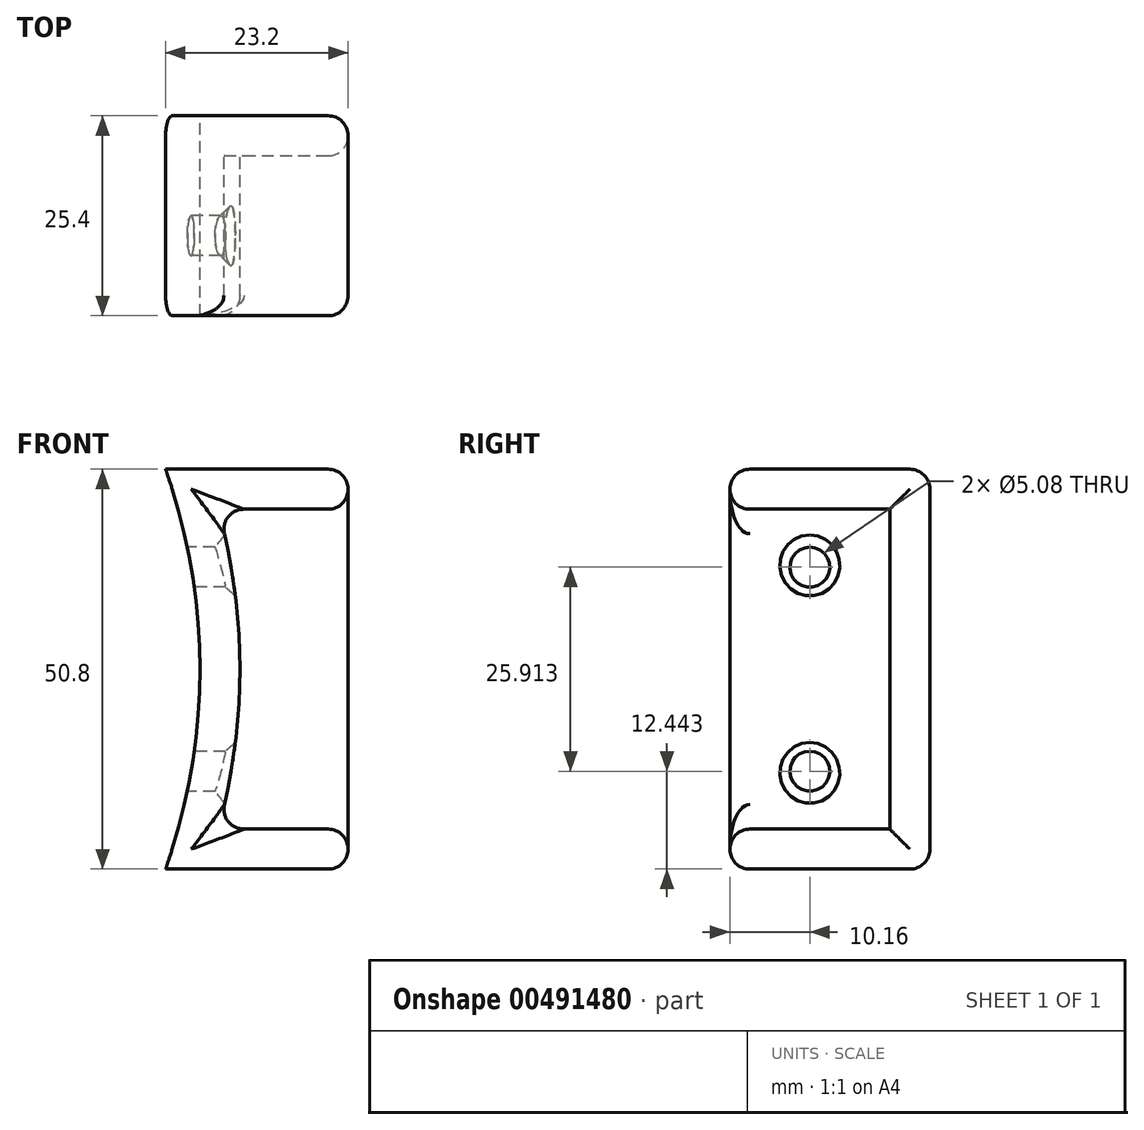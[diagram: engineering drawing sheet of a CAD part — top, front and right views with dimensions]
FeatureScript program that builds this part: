
annotation { "Feature Type Name" : "Feature", "Feature Type Description" : "" }
export const myFeature = defineFeature(function(context is Context, id is Id, definition is map)
    precondition{}
    {
        {
            var Q0;
            Q0=qCreatedBy(makeId("Front.planeOp"),FACE);
            var sketch = newSketch(context, id + "F0", { "sketchPlane" : qUnion([Q0])});
            skArc(sketch, "E0", {"start": v(71.84, -25.4) * mm, "mid": v(76.2, 0) * mm, "end": v(71.84, 25.4) * mm});
            skLineSegment(sketch, "E1", {"start": v(71.84, 25.4) * mm, "end": v(95.04, 25.4) * mm});
            skLineSegment(sketch, "E2", {"start": v(95.04, 25.4) * mm, "end": v(95.04, -25.4) * mm});
            skLineSegment(sketch, "E3", {"start": v(95.04, -25.4) * mm, "end": v(71.84, -25.4) * mm});
            skArc(sketch, "E4", {"start": v(78.52, -20.32) * mm, "mid": v(81.28, 0) * mm, "end": v(78.52, 20.32) * mm});
            skLineSegment(sketch, "E5", {"start": v(78.52, -20.32) * mm, "end": v(95.04, -20.32) * mm});
            skLineSegment(sketch, "E6", {"start": v(78.52, 20.32) * mm, "end": v(95.04, 20.32) * mm});
            skPoint(sketch, "E7.orphan", {"position": v(76.92, 25.4) * mm});
            skPoint(sketch, "E8.orphan", {"position": v(76.92, -25.4) * mm});
            skSolve(sketch);
        }
        {
            var Q0;
            Q0=makeQuery(id+"F0.imprint","IMPRINT",FACE,{"disambiguationData":[TD([[makeQuery(id+"F0.imprint","IMPRINT",EDGE,{"derivedFrom":sQuery(id+"F0.wireOp",EDGE,"E0")}),-1.0]])]});
            extrude(context, id + "F1", {"entities" : qUnion([Q0]), "depth" : 25.4 * mm});
        }
        {
            var Q0;
            Q0=makeQuery(id+"F0.imprint","IMPRINT",FACE,{"disambiguationData":[TD([[makeQuery(id+"F0.imprint","IMPRINT",EDGE,{"derivedFrom":sQuery(id+"F0.wireOp",EDGE,"E4")}),-1.0]])]});
            extrude(context, id + "F2", {"entities" : qUnion([Q0]), "operationType" : NewBodyOperationType.ADD, "depth" : 5.08 * mm});
        }
        {
            var Q0;
            Q0=makeQuery(id+"F2.opExtrude","CAP_EDGE",EDGE,{"disambiguationData":[OSD([sQuery(id+"F0.wireOp",EDGE,"E2")])],"isStart":false});
            fillet(context, id + "F3", {"entities" : qUnion([Q0]), "radius" : 2.54 * mm, "tangentPropagation" : true, "allowEdgeOverflow" : false});
        }
        {
            var Q0;
            Q0=makeQuery(id+"F1.opExtrude","SWEPT_EDGE",EDGE,{"disambiguationData":[OSD([sQuery(id+"F0.wireOp",EDGE,"E2"),sQuery(id+"F0.wireOp",EDGE,"E5")])]});
            var Q1;
            {var subQ0=sQuery(id+"F0.wireOp",EDGE,"E2");Q1=makeQuery(id+"F1.opExtrude","CAP_EDGE",EDGE,{"disambiguationData":[OSD([subQ0]),TDD([makeQuery(id+"F0.imprint","IMPRINT",EDGE,{"disambiguationData":[TD([[makeQuery(id+"F0.imprint","INTERSECT",VERTEX,{"derivedFrom":[subQ0,sQuery(id+"F0.wireOp",EDGE,"E3")]}),1.0]])],"derivedFrom":subQ0})])],"isStart":false});}
            var Q2;
            Q2=makeQuery(id+"F1.opExtrude","SWEPT_EDGE",EDGE,{"disambiguationData":[OSD([sQuery(id+"F0.wireOp",EDGE,"E2"),sQuery(id+"F0.wireOp",EDGE,"E3")])]});
            var Q3;
            Q3=makeQuery(id+"F1.opExtrude","SWEPT_EDGE",EDGE,{"disambiguationData":[OSD([sQuery(id+"F0.wireOp",EDGE,"E1"),sQuery(id+"F0.wireOp",EDGE,"E2")])]});
            var Q4;
            {var subQ0=sQuery(id+"F0.wireOp",EDGE,"E2");Q4=makeQuery(id+"F1.opExtrude","CAP_EDGE",EDGE,{"disambiguationData":[OSD([subQ0]),TDD([makeQuery(id+"F0.imprint","IMPRINT",EDGE,{"disambiguationData":[TD([[makeQuery(id+"F0.imprint","INTERSECT",VERTEX,{"derivedFrom":[sQuery(id+"F0.wireOp",EDGE,"E1"),subQ0]}),-1.0]])],"derivedFrom":subQ0})])],"isStart":false});}
            var Q5;
            Q5=makeQuery(id+"F1.opExtrude","SWEPT_EDGE",EDGE,{"disambiguationData":[OSD([sQuery(id+"F0.wireOp",EDGE,"E2"),sQuery(id+"F0.wireOp",EDGE,"E6")])]});
            var Q6;
            Q6=makeQuery(id+"F1.opExtrude","CAP_EDGE",EDGE,{"disambiguationData":[OSD([sQuery(id+"F0.wireOp",EDGE,"E1")])],"isStart":true});
            var Q7;
            Q7=makeQuery(id+"F1.opExtrude","CAP_EDGE",EDGE,{"disambiguationData":[OSD([sQuery(id+"F0.wireOp",EDGE,"E3")])],"isStart":true});
            var Q8;
            Q8=makeQuery(id+"F1.opExtrude","CAP_EDGE",EDGE,{"disambiguationData":[OSD([sQuery(id+"F0.wireOp",EDGE,"E3")])],"isStart":false});
            var Q9;
            Q9=makeQuery(id+"F1.opExtrude","CAP_EDGE",EDGE,{"disambiguationData":[OSD([sQuery(id+"F0.wireOp",EDGE,"E5")])],"isStart":false});
            var Q10;
            Q10=makeQuery(id+"F1.opExtrude","CAP_EDGE",EDGE,{"disambiguationData":[OSD([sQuery(id+"F0.wireOp",EDGE,"E6")])],"isStart":false});
            var Q11;
            Q11=makeQuery(id+"F1.opExtrude","CAP_EDGE",EDGE,{"disambiguationData":[OSD([sQuery(id+"F0.wireOp",EDGE,"E1")])],"isStart":false});
            var Q12;
            Q12=makeQuery(id+"F1.opExtrude","CAP_EDGE",EDGE,{"disambiguationData":[OSD([sQuery(id+"F0.wireOp",EDGE,"E4")])],"isStart":false});
            fillet(context, id + "F4", {"entities" : qUnion([Q0, Q1, Q2, Q3, Q4, Q5, Q6, Q7, Q8, Q9, Q10, Q11, Q12]), "radius" : 2.54 * mm, "tangentPropagation" : true, "allowEdgeOverflow" : false});
        }
        {
            var Q0;
            Q0=makeQuery(id+"F1.opExtrude","SWEPT_EDGE",EDGE,{"disambiguationData":[OSD([sQuery(id+"F0.wireOp",EDGE,"E4"),sQuery(id+"F0.wireOp",EDGE,"E6")])]});
            var Q1;
            Q1=makeQuery(id+"F1.opExtrude","SWEPT_EDGE",EDGE,{"disambiguationData":[OSD([sQuery(id+"F0.wireOp",EDGE,"E4"),sQuery(id+"F0.wireOp",EDGE,"E5")])]});
            var Q2;
            Q2=makeQuery(id+"F2.opExtrude","CAP_EDGE",EDGE,{"disambiguationData":[OSD([sQuery(id+"F0.wireOp",EDGE,"E4")])],"isStart":false});
            var Q3;
            {var subQ0=sQuery(id+"F0.wireOp",EDGE,"E2");Q3=makeQuery(id+"F2.boolean.opBoolean","MERGE",EDGE,{"derivedFrom":[makeQuery(id+"F1.opExtrude","CAP_EDGE",EDGE,{"disambiguationData":[OSD([subQ0]),TDD([makeQuery(id+"F0.imprint","IMPRINT",EDGE,{"disambiguationData":[TD([[makeQuery(id+"F0.imprint","INTERSECT",VERTEX,{"derivedFrom":[sQuery(id+"F0.wireOp",EDGE,"E1"),subQ0]}),-1.0]])],"derivedFrom":subQ0})])],"isStart":true}),makeQuery(id+"F1.opExtrude","CAP_EDGE",EDGE,{"disambiguationData":[OSD([subQ0]),TDD([makeQuery(id+"F0.imprint","IMPRINT",EDGE,{"disambiguationData":[TD([[makeQuery(id+"F0.imprint","INTERSECT",VERTEX,{"derivedFrom":[subQ0,sQuery(id+"F0.wireOp",EDGE,"E3")]}),1.0]])],"derivedFrom":subQ0})])],"isStart":true}),makeQuery(id+"F2.opExtrude","CAP_EDGE",EDGE,{"disambiguationData":[OSD([subQ0])],"isStart":true})]});}
            fillet(context, id + "F5", {"entities" : qUnion([Q0, Q1, Q2, Q3]), "radius" : 2.54 * mm, "tangentPropagation" : true, "allowEdgeOverflow" : false});
        }
        {
            var Q0;
            Q0=qCreatedBy(makeId("Right.planeOp"),FACE);
            var sketch = newSketch(context, id + "F6", { "sketchPlane" : qUnion([Q0])});
            skCircle(sketch, "E9", {"center": v(-15.24, 12.96) * mm, "radius": 2.54 * mm});
            skCircle(sketch, "E10", {"center": v(-15.24, -12.96) * mm, "radius": 2.54 * mm});
            skSolve(sketch);
        }
        {
            var Q0;
            Q0=makeQuery(id+"F6.imprint","IMPRINT",FACE,{"disambiguationData":[TD([[makeQuery(id+"F6.imprint","IMPRINT",EDGE,{"derivedFrom":sQuery(id+"F6.wireOp",EDGE,"E9")}),1.0]])]});
            extrude(context, id + "F7", {"entities" : qUnion([Q0]), "operationType" : NewBodyOperationType.REMOVE, "depth" : 106.17 * mm});
        }
        {
            var Q0;
            Q0=makeQuery(id+"F6.imprint","IMPRINT",FACE,{"disambiguationData":[TD([[makeQuery(id+"F6.imprint","IMPRINT",EDGE,{"derivedFrom":sQuery(id+"F6.wireOp",EDGE,"E10")}),1.0]])]});
            extrude(context, id + "F8", {"entities" : qUnion([Q0]), "operationType" : NewBodyOperationType.REMOVE, "depth" : 97.28 * mm});
        }
        {
            var Q0;
            Q0=makeQuery(id+"F7.boolean.opBoolean","INTERSECT",EDGE,{"derivedFrom":[makeQuery(id+"F1.opExtrude","SWEPT_FACE",FACE,{"disambiguationData":[OSD([sQuery(id+"F0.wireOp",EDGE,"E4")])]}),makeQuery(id+"F7.opExtrude","SWEPT_FACE",FACE,{"disambiguationData":[OSD([sQuery(id+"F6.wireOp",EDGE,"E9")])]})]});
            var Q1;
            Q1=makeQuery(id+"F8.boolean.opBoolean","INTERSECT",EDGE,{"derivedFrom":[makeQuery(id+"F1.opExtrude","SWEPT_FACE",FACE,{"disambiguationData":[OSD([sQuery(id+"F0.wireOp",EDGE,"E4")])]}),makeQuery(id+"F8.opExtrude","SWEPT_FACE",FACE,{"disambiguationData":[OSD([sQuery(id+"F6.wireOp",EDGE,"E10")])]})]});
            chamfer(context, id + "F9", {"entities" : qUnion([Q0, Q1]), "width" : 1.27 * mm, "tangentPropagation" : true});
        }
    });
